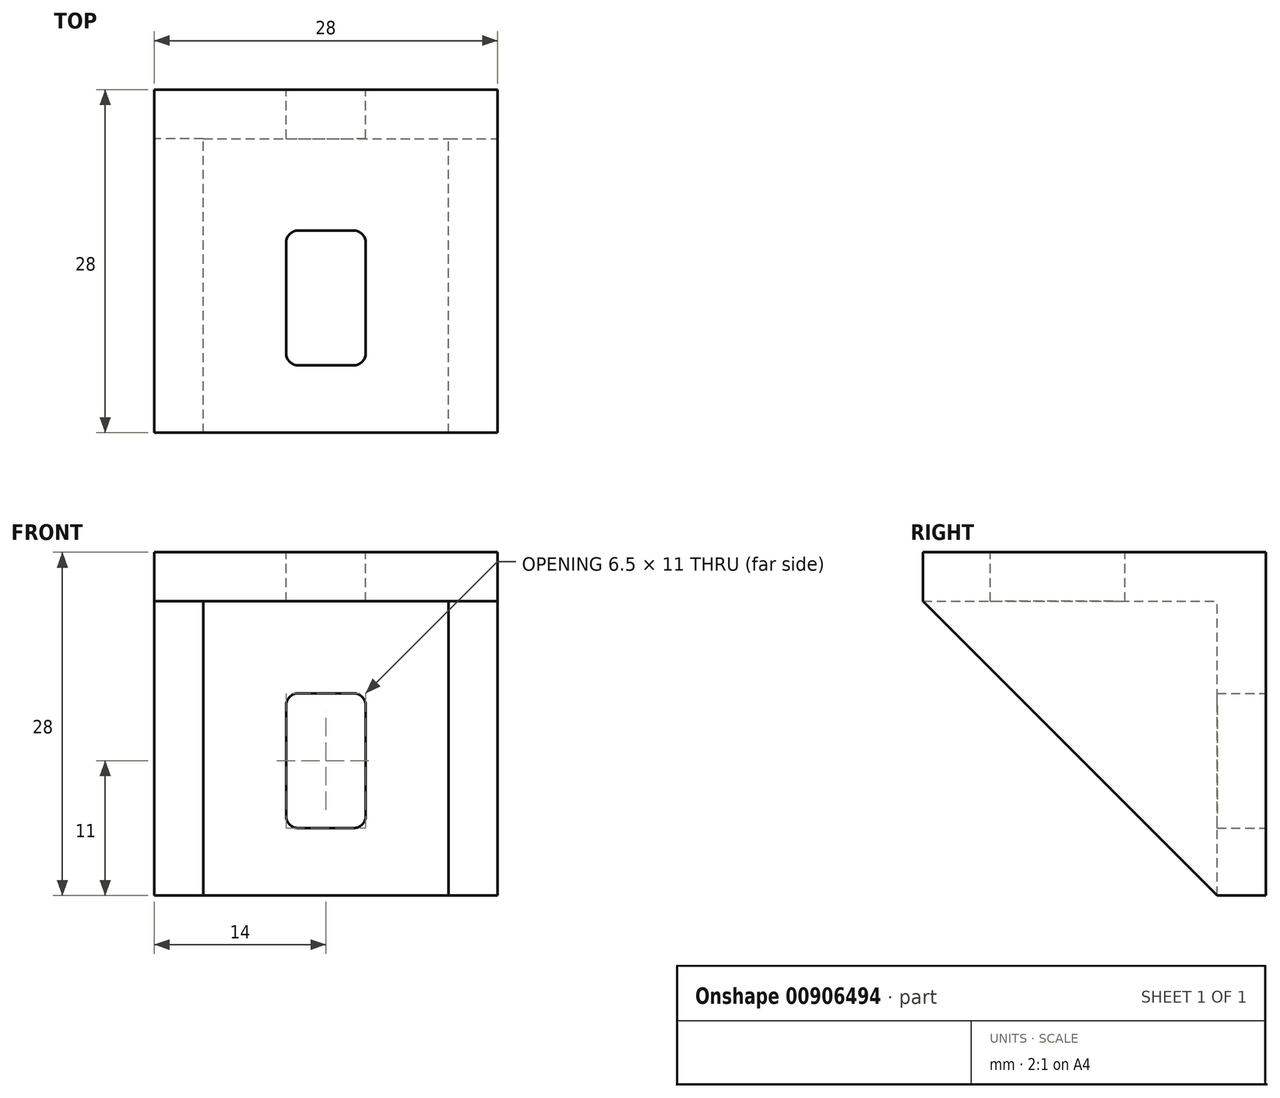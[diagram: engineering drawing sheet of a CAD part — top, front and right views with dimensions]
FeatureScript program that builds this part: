
annotation { "Feature Type Name" : "Feature", "Feature Type Description" : "" }
export const myFeature = defineFeature(function(context is Context, id is Id, definition is map)
    precondition{}
    {
        {
            var Q0;
            Q0=qCreatedBy(makeId("Front.planeOp"),FACE);
            var sketch = newSketch(context, id + "F0", { "sketchPlane" : qUnion([Q0])});
            skLineSegment(sketch, "E0", {"start": v(0, 0) * mm, "end": v(14, 0) * mm});
            skLineSegment(sketch, "E1", {"start": v(0, 0) * mm, "end": v(-14, 0) * mm});
            skLineSegment(sketch, "E2", {"start": v(-14, 0) * mm, "end": v(-14, 28) * mm});
            skLineSegment(sketch, "E3", {"start": v(-14, 28) * mm, "end": v(14, 28) * mm});
            skLineSegment(sketch, "E4", {"start": v(14, 28) * mm, "end": v(14, 0) * mm});
            skPoint(sketch, "E5", {"position": v(-10, 0) * mm});
            skPoint(sketch, "E6", {"position": v(-10, 24) * mm});
            skPoint(sketch, "E7", {"position": v(10, 0) * mm});
            skPoint(sketch, "E8", {"position": v(10, 24) * mm});
            skLineSegment(sketch, "E9", {"start": v(-10, 0) * mm, "end": v(-10, 24) * mm});
            skLineSegment(sketch, "E10", {"start": v(-10, 24) * mm, "end": v(10, 24) * mm});
            skLineSegment(sketch, "E11", {"start": v(10, 24) * mm, "end": v(10, 0) * mm});
            skPoint(sketch, "E12", {"position": v(0, 5.5) * mm});
            skPoint(sketch, "E12.positionSnap0", {"position": v(0, 28) * mm});
            skPoint(sketch, "E13", {"position": v(0, 16.5) * mm});
            skPoint(sketch, "E14", {"position": v(3.25, 16.5) * mm});
            skPoint(sketch, "E15", {"position": v(3.25, 5.5) * mm});
            skPoint(sketch, "E16", {"position": v(-3.25, 16.5) * mm});
            skPoint(sketch, "E17", {"position": v(-3.25, 5.5) * mm});
            skLineSegment(sketch, "E18", {"start": v(0, 5.5) * mm, "end": v(2.25, 5.5) * mm});
            skLineSegment(sketch, "E19", {"start": v(2.25, 16.5) * mm, "end": v(0, 16.5) * mm});
            skLineSegment(sketch, "E20", {"start": v(-2.25, 16.5) * mm, "end": v(0, 16.5) * mm});
            skLineSegment(sketch, "E21", {"start": v(-3.25, 6.5) * mm, "end": v(-3.25, 15.5) * mm});
            skLineSegment(sketch, "E22", {"start": v(3.25, 15.5) * mm, "end": v(3.25, 6.5) * mm});
            skArc(sketch, "E23.filletArc", {"start": v(-2.25, 16.5) * mm, "mid": v(-2.96, 16.2) * mm, "end": v(-3.25, 15.5) * mm});
            skArc(sketch, "E24.filletArc", {"start": v(3.25, 15.5) * mm, "mid": v(2.96, 16.2) * mm, "end": v(2.25, 16.5) * mm});
            skArc(sketch, "E25.filletArc", {"start": v(2.25, 5.5) * mm, "mid": v(2.96, 5.8) * mm, "end": v(3.25, 6.5) * mm});
            skLineSegment(sketch, "E26", {"start": v(0, 5.5) * mm, "end": v(-2.25, 5.5) * mm});
            skArc(sketch, "E27.filletArc", {"start": v(-3.25, 6.5) * mm, "mid": v(-2.96, 5.8) * mm, "end": v(-2.25, 5.5) * mm});
            skSolve(sketch);
        }
        {
            var Q0;
            {var subQ0=sQuery(id+"F0.wireOp",EDGE,"E2");Q0=makeQuery(id+"F0.imprint","IMPRINT",FACE,{"disambiguationData":[TD([[makeQuery(id+"F0.imprint","IMPRINT",EDGE,{"derivedFrom":subQ0}),-1.0]])]});}
            extrude(context, id + "F1", {"entities" : qUnion([Q0]), "depth" : 28 * mm, "offsetDistance" : 25 * mm});
        }
        {
            var Q0;
            {var subQ0=sQuery(id+"F0.wireOp",EDGE,"E9");Q0=makeQuery(id+"F0.imprint","IMPRINT",FACE,{"disambiguationData":[TD([[makeQuery(id+"F0.imprint","IMPRINT",EDGE,{"derivedFrom":subQ0}),-1.0]])]});}
            extrude(context, id + "F2", {"entities" : qUnion([Q0]), "operationType" : NewBodyOperationType.ADD, "depth" : 4 * mm, "offsetDistance" : 25 * mm});
        }
        {
            var Q0;
            Q0=makeQuery(id+"F1.opExtrude","SWEPT_FACE",FACE,{"disambiguationData":[OSD([sQuery(id+"F0.wireOp",EDGE,"E4")])]});
            var sketch = newSketch(context, id + "F3", { "sketchPlane" : qUnion([Q0])});
            skLineSegment(sketch, "E28", {"start": v(-28, 24) * mm, "end": v(-4, 0) * mm});
            skSolve(sketch);
        }
        {
            var Q0;
            {var subQ0=sQuery(id+"F3.wireOp",EDGE,"E28");Q0=makeQuery(id+"F3.imprint","IMPRINT",FACE,{"disambiguationData":[TD([[makeQuery(id+"F3.imprint","IMPRINT",EDGE,{"derivedFrom":subQ0}),-1.0]])]});}
            extrude(context, id + "F4", {"entities" : qUnion([Q0]), "operationType" : NewBodyOperationType.REMOVE, "oppositeDirection" : true, "depth" : 4 * mm, "offsetDistance" : 25 * mm});
        }
        {
            var Q0;
            Q0=makeQuery(id+"F1.opExtrude","SWEPT_FACE",FACE,{"disambiguationData":[OSD([sQuery(id+"F0.wireOp",EDGE,"E2")])]});
            var sketch = newSketch(context, id + "F5", { "sketchPlane" : qUnion([Q0])});
            skPoint(sketch, "E29", {"position": v(28, 24) * mm});
            skPoint(sketch, "E30", {"position": v(4, 0) * mm});
            skLineSegment(sketch, "E31", {"start": v(4, 0) * mm, "end": v(28, 24) * mm});
            skSolve(sketch);
        }
        {
            var Q0;
            {var subQ0=sQuery(id+"F5.wireOp",EDGE,"E31");Q0=makeQuery(id+"F5.imprint","IMPRINT",FACE,{"disambiguationData":[TD([[makeQuery(id+"F5.imprint","IMPRINT",EDGE,{"derivedFrom":subQ0}),-1.0]])]});}
            extrude(context, id + "F6", {"entities" : qUnion([Q0]), "operationType" : NewBodyOperationType.REMOVE, "oppositeDirection" : true, "depth" : 4 * mm, "offsetDistance" : 25 * mm});
        }
        {
            var Q0;
            Q0=makeQuery(id+"F0.imprint","IMPRINT",FACE,{"disambiguationData":[TD([[makeQuery(id+"F0.imprint","IMPRINT",EDGE,{"derivedFrom":sQuery(id+"F0.wireOp",EDGE,"E18")}),1.0]])]});
            extrude(context, id + "F7", {"entities" : qUnion([Q0]), "operationType" : NewBodyOperationType.REMOVE, "depth" : 4 * mm, "offsetDistance" : 25 * mm});
        }
        {
            var Q0;
            Q0=makeQuery(id+"F1.opExtrude","SWEPT_FACE",FACE,{"disambiguationData":[OSD([sQuery(id+"F0.wireOp",EDGE,"E3")])]});
            var sketch = newSketch(context, id + "F8", { "sketchPlane" : qUnion([Q0])});
            skPoint(sketch, "E32", {"position": v(0, -22.5) * mm});
            skPoint(sketch, "E32.positionSnap0", {"position": v(0, 0) * mm});
            skPoint(sketch, "E33", {"position": v(0, -11.5) * mm});
            skPoint(sketch, "E34", {"position": v(-3.25, -22.5) * mm});
            skPoint(sketch, "E35", {"position": v(3.25, -22.5) * mm});
            skPoint(sketch, "E36", {"position": v(-3.25, -11.5) * mm});
            skPoint(sketch, "E37", {"position": v(3.25, -11.5) * mm});
            skLineSegment(sketch, "E38", {"start": v(-3.25, -21.5) * mm, "end": v(-3.25, -12.5) * mm});
            skLineSegment(sketch, "E39", {"start": v(-2.25, -11.5) * mm, "end": v(2.25, -11.5) * mm});
            skLineSegment(sketch, "E40", {"start": v(3.25, -12.5) * mm, "end": v(3.25, -21.5) * mm});
            skLineSegment(sketch, "E41", {"start": v(2.25, -22.5) * mm, "end": v(-2.25, -22.5) * mm});
            skArc(sketch, "E42.filletArc", {"start": v(-3.25, -21.5) * mm, "mid": v(-2.96, -22.2) * mm, "end": v(-2.25, -22.5) * mm});
            skArc(sketch, "E43.filletArc", {"start": v(2.25, -22.5) * mm, "mid": v(2.96, -22.2) * mm, "end": v(3.25, -21.5) * mm});
            skArc(sketch, "E44.filletArc", {"start": v(3.25, -12.5) * mm, "mid": v(2.96, -11.8) * mm, "end": v(2.25, -11.5) * mm});
            skArc(sketch, "E45.filletArc", {"start": v(-2.25, -11.5) * mm, "mid": v(-2.96, -11.8) * mm, "end": v(-3.25, -12.5) * mm});
            skSolve(sketch);
        }
        {
            var Q0;
            Q0=makeQuery(id+"F8.imprint","IMPRINT",FACE,{"disambiguationData":[TD([[makeQuery(id+"F8.imprint","IMPRINT",EDGE,{"derivedFrom":sQuery(id+"F8.wireOp",EDGE,"E38")}),-1.0]])]});
            extrude(context, id + "F9", {"entities" : qUnion([Q0]), "operationType" : NewBodyOperationType.REMOVE, "oppositeDirection" : true, "depth" : 4 * mm, "offsetDistance" : 25 * mm});
        }
    });
